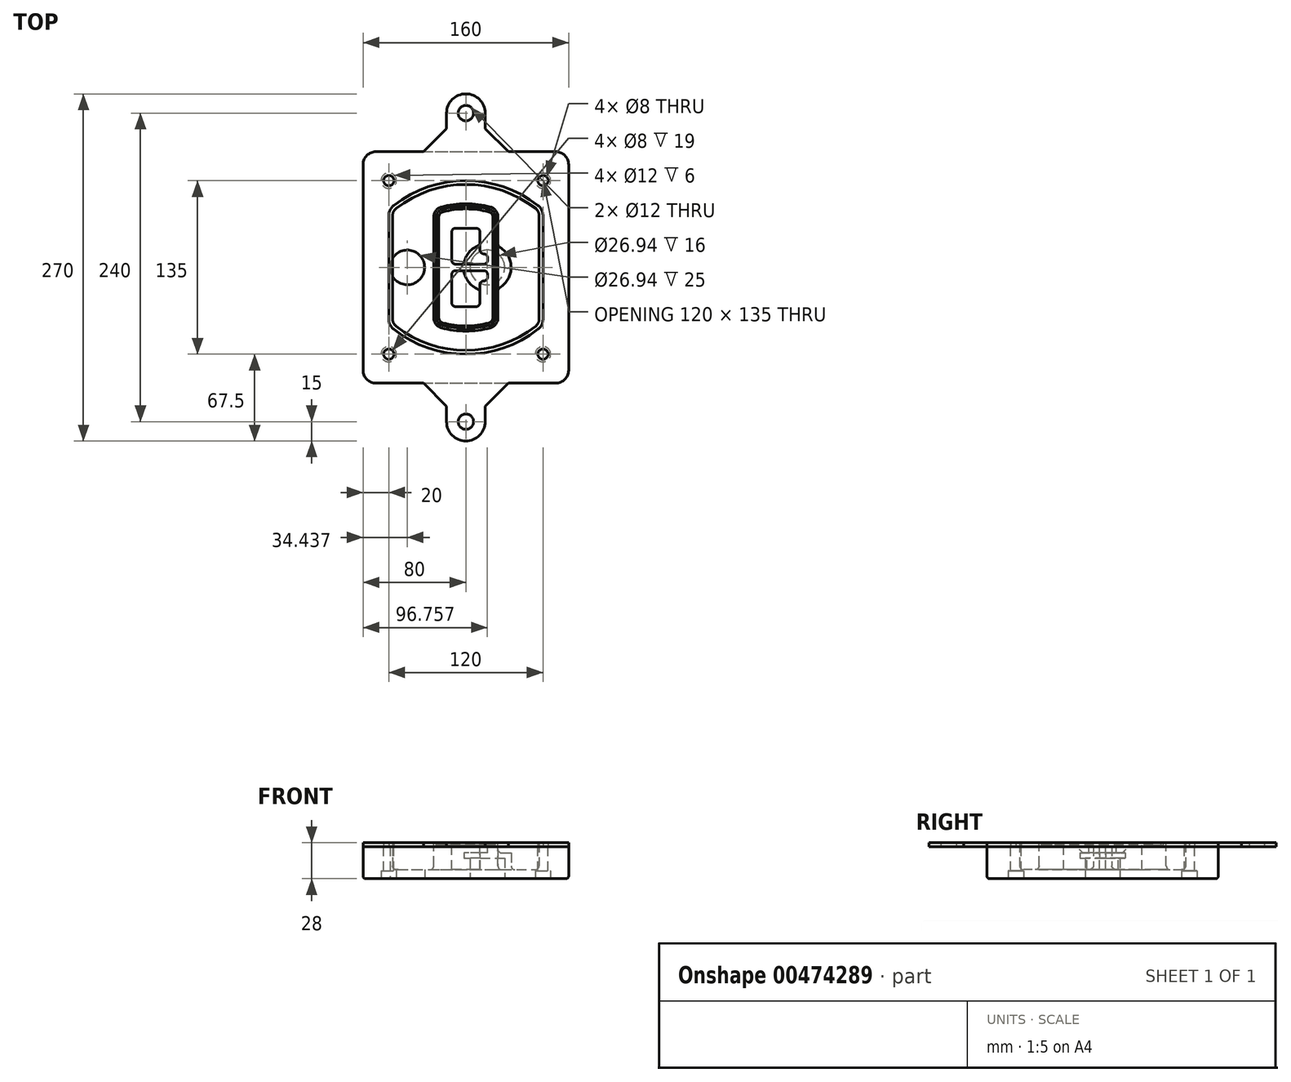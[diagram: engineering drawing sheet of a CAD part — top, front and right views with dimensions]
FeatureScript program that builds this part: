
annotation { "Feature Type Name" : "Feature", "Feature Type Description" : "" }
export const myFeature = defineFeature(function(context is Context, id is Id, definition is map)
    precondition{}
    {
        {
            var Q0;
            Q0=qCreatedBy(makeId("Top.planeOp"),FACE);
            var sketch = newSketch(context, id + "F0", { "sketchPlane" : qUnion([Q0])});
            skPoint(sketch, "E0.rect.middle", {"position": v(0, 0) * mm});
            skLineSegment(sketch, "E1.bottom", {"start": v(-70, -90) * mm, "end": v(70, -90) * mm});
            skLineSegment(sketch, "E1.top", {"start": v(-70, 90) * mm, "end": v(70, 90) * mm});
            skLineSegment(sketch, "E1.left", {"start": v(-80, -80) * mm, "end": v(-80, 80) * mm});
            skLineSegment(sketch, "E1.right", {"start": v(80, -80) * mm, "end": v(80, 80) * mm});
            skLineSegment(sketch, "E2", {"start": v(-80, 90) * mm, "end": v(80, -90) * mm, "construction": true});
            skLineSegment(sketch, "E3", {"start": v(80, 90) * mm, "end": v(-80, -90) * mm, "construction": true});
            skCircle(sketch, "E4", {"center": v(-60, 67.5) * mm, "radius": 4 * mm});
            skCircle(sketch, "E5", {"center": v(60, 67.5) * mm, "radius": 4 * mm});
            skCircle(sketch, "E6", {"center": v(60, -67.5) * mm, "radius": 4 * mm});
            skCircle(sketch, "E7", {"center": v(-60, -67.5) * mm, "radius": 4 * mm});
            skLineSegment(sketch, "E8", {"start": v(-60, 67.5) * mm, "end": v(60, 67.5) * mm, "construction": true});
            skLineSegment(sketch, "E9", {"start": v(60, 67.5) * mm, "end": v(60, -67.5) * mm, "construction": true});
            skLineSegment(sketch, "E10", {"start": v(60, -67.5) * mm, "end": v(-60, -67.5) * mm, "construction": true});
            skLineSegment(sketch, "E11", {"start": v(-60, -67.5) * mm, "end": v(-60, 67.5) * mm, "construction": true});
            skLineSegment(sketch, "E12", {"start": v(-60, 40.3) * mm, "end": v(-60, -40.3) * mm});
            skLineSegment(sketch, "E13", {"start": v(60, 40.3) * mm, "end": v(60, -40.3) * mm});
            skArc(sketch, "E14", {"start": v(56.15, 48.18) * mm, "mid": v(0, 67.5) * mm, "end": v(-56.15, 48.18) * mm});
            skArc(sketch, "E15", {"start": v(-56.15, -48.18) * mm, "mid": v(0, -67.5) * mm, "end": v(56.15, -48.18) * mm});
            skLineSegment(sketch, "E16", {"start": v(-60, 0) * mm, "end": v(60, 0) * mm, "construction": true});
            skPoint(sketch, "E17.visualSharp", {"position": v(-60, -45) * mm});
            skArc(sketch, "E17.filletArc", {"start": v(-60, -40.3) * mm, "mid": v(-58.99, -44.68) * mm, "end": v(-56.15, -48.18) * mm});
            skPoint(sketch, "E18.visualSharp", {"position": v(-60, 45) * mm});
            skArc(sketch, "E18.filletArc", {"start": v(-56.15, 48.18) * mm, "mid": v(-58.99, 44.68) * mm, "end": v(-60, 40.3) * mm});
            skPoint(sketch, "E19.visualSharp", {"position": v(60, 45) * mm});
            skArc(sketch, "E19.filletArc", {"start": v(60, 40.3) * mm, "mid": v(58.99, 44.68) * mm, "end": v(56.15, 48.18) * mm});
            skPoint(sketch, "E20.visualSharp", {"position": v(60, -45) * mm});
            skArc(sketch, "E20.filletArc", {"start": v(56.15, -48.18) * mm, "mid": v(58.99, -44.68) * mm, "end": v(60, -40.3) * mm});
            skPoint(sketch, "E21.visualSharp", {"position": v(-80, 90) * mm});
            skArc(sketch, "E21.filletArc", {"start": v(-70, 90) * mm, "mid": v(-77.07, 87.07) * mm, "end": v(-80, 80) * mm});
            skPoint(sketch, "E22.visualSharp", {"position": v(80, 90) * mm});
            skArc(sketch, "E22.filletArc", {"start": v(80, 80) * mm, "mid": v(77.07, 87.07) * mm, "end": v(70, 90) * mm});
            skPoint(sketch, "E23.visualSharp", {"position": v(80, -90) * mm});
            skArc(sketch, "E23.filletArc", {"start": v(70, -90) * mm, "mid": v(77.07, -87.07) * mm, "end": v(80, -80) * mm});
            skPoint(sketch, "E24.visualSharp", {"position": v(-80, -90) * mm});
            skArc(sketch, "E24.filletArc", {"start": v(-80, -80) * mm, "mid": v(-77.07, -87.07) * mm, "end": v(-70, -90) * mm});
            skArc(sketch, "E25.0", {"start": v(57, 40.3) * mm, "mid": v(56.3, 43.36) * mm, "end": v(54.3, 45.81) * mm});
            skLineSegment(sketch, "E25.1", {"start": v(57, 40.3) * mm, "end": v(57, -40.3) * mm});
            skArc(sketch, "E25.2", {"start": v(54.3, -45.81) * mm, "mid": v(56.3, -43.36) * mm, "end": v(57, -40.3) * mm});
            skArc(sketch, "E25.3", {"start": v(-54.3, -45.81) * mm, "mid": v(0, -64.5) * mm, "end": v(54.3, -45.81) * mm});
            skArc(sketch, "E25.4", {"start": v(-57, -40.3) * mm, "mid": v(-56.3, -43.36) * mm, "end": v(-54.3, -45.81) * mm});
            skArc(sketch, "E25.5", {"start": v(54.3, 45.81) * mm, "mid": v(0, 64.5) * mm, "end": v(-54.3, 45.81) * mm});
            skLineSegment(sketch, "E25.6", {"start": v(-57, 40.3) * mm, "end": v(-57, -40.3) * mm});
            skArc(sketch, "E25.7", {"start": v(-54.3, 45.81) * mm, "mid": v(-56.3, 43.36) * mm, "end": v(-57, 40.3) * mm});
            skArc(sketch, "E26.0", {"start": v(-58.62, 51.33) * mm, "mid": v(-62.58, 46.43) * mm, "end": v(-64, 40.3) * mm});
            skArc(sketch, "E26.1", {"start": v(58.62, 51.33) * mm, "mid": v(0, 71.5) * mm, "end": v(-58.62, 51.33) * mm});
            skArc(sketch, "E26.2", {"start": v(64, 40.3) * mm, "mid": v(62.58, 46.43) * mm, "end": v(58.62, 51.33) * mm});
            skLineSegment(sketch, "E26.3", {"start": v(64, 40.3) * mm, "end": v(64, -40.3) * mm});
            skArc(sketch, "E26.4", {"start": v(58.62, -51.33) * mm, "mid": v(62.58, -46.43) * mm, "end": v(64, -40.3) * mm});
            skLineSegment(sketch, "E26.5", {"start": v(-64, 40.3) * mm, "end": v(-64, -40.3) * mm});
            skArc(sketch, "E26.6", {"start": v(-58.62, -51.33) * mm, "mid": v(0, -71.5) * mm, "end": v(58.62, -51.33) * mm});
            skArc(sketch, "E26.7", {"start": v(-64, -40.3) * mm, "mid": v(-62.58, -46.43) * mm, "end": v(-58.62, -51.33) * mm});
            skSolve(sketch);
        }
        {
            var Q0;
            Q0=makeQuery(id+"F0.imprint","IMPRINT",FACE,{"disambiguationData":[TD([[makeQuery(id+"F0.imprint","IMPRINT",EDGE,{"derivedFrom":sQuery(id+"F0.wireOp",EDGE,"E1.bottom")}),1.0]])]});
            var Q1;
            Q1=makeQuery(id+"F0.imprint","IMPRINT",FACE,{"disambiguationData":[TD([[makeQuery(id+"F0.imprint","IMPRINT",EDGE,{"derivedFrom":sQuery(id+"F0.wireOp",EDGE,"E12")}),1.0]])]});
            var Q2;
            Q2=makeQuery(id+"F0.imprint","IMPRINT",FACE,{"disambiguationData":[TD([[makeQuery(id+"F0.imprint","IMPRINT",EDGE,{"derivedFrom":sQuery(id+"F0.wireOp",EDGE,"E25.0")}),1.0]])]});
            var Q3;
            Q3=makeQuery(id+"F0.imprint","IMPRINT",FACE,{"disambiguationData":[TD([[makeQuery(id+"F0.imprint","IMPRINT",EDGE,{"derivedFrom":sQuery(id+"F0.wireOp",EDGE,"E12")}),-1.0]])]});
            extrude(context, id + "F1", {"entities" : qUnion([Q0, Q1, Q2, Q3]), "oppositeDirection" : true, "depth" : 25 * mm});
        }
        {
            var Q0;
            Q0=makeQuery(id+"F0.imprint","IMPRINT",FACE,{"disambiguationData":[TD([[makeQuery(id+"F0.imprint","IMPRINT",EDGE,{"derivedFrom":sQuery(id+"F0.wireOp",EDGE,"E12")}),1.0]])]});
            extrude(context, id + "F2", {"entities" : qUnion([Q0]), "operationType" : NewBodyOperationType.ADD, "depth" : 3 * mm});
        }
        {
            var Q0;
            Q0=makeQuery(id+"F0.imprint","IMPRINT",FACE,{"disambiguationData":[TD([[makeQuery(id+"F0.imprint","IMPRINT",EDGE,{"derivedFrom":sQuery(id+"F0.wireOp",EDGE,"E25.0")}),1.0]])]});
            extrude(context, id + "F3", {"entities" : qUnion([Q0]), "operationType" : NewBodyOperationType.REMOVE, "oppositeDirection" : true, "depth" : 18 * mm});
        }
        {
            var Q0;
            Q0=makeQuery(id+"F2.opExtrude","CAP_FACE",FACE,{"disambiguationData":[OSD([sQuery(id+"F0.wireOp",EDGE,"E12"),sQuery(id+"F0.wireOp",EDGE,"E13"),sQuery(id+"F0.wireOp",EDGE,"E14"),sQuery(id+"F0.wireOp",EDGE,"E15"),sQuery(id+"F0.wireOp",EDGE,"E17.filletArc"),sQuery(id+"F0.wireOp",EDGE,"E18.filletArc"),sQuery(id+"F0.wireOp",EDGE,"E19.filletArc"),sQuery(id+"F0.wireOp",EDGE,"E20.filletArc"),sQuery(id+"F0.wireOp",EDGE,"E25.0"),sQuery(id+"F0.wireOp",EDGE,"E25.1"),sQuery(id+"F0.wireOp",EDGE,"E25.2"),sQuery(id+"F0.wireOp",EDGE,"E25.3"),sQuery(id+"F0.wireOp",EDGE,"E25.4"),sQuery(id+"F0.wireOp",EDGE,"E25.5"),sQuery(id+"F0.wireOp",EDGE,"E25.6"),sQuery(id+"F0.wireOp",EDGE,"E25.7")])],"isStart":false});
            var sketch = newSketch(context, id + "F4", { "sketchPlane" : qUnion([Q0])});
            skArc(sketch, "E27.0", {"start": v(-19.08, -46.97) * mm, "mid": v(0, -49.5) * mm, "end": v(19.08, -46.97) * mm});
            skArc(sketch, "E28.0", {"start": v(19.08, 46.97) * mm, "mid": v(0, 49.5) * mm, "end": v(-19.08, 46.97) * mm});
            skLineSegment(sketch, "E29", {"start": v(-25, 39.25) * mm, "end": v(-25, -39.25) * mm});
            skLineSegment(sketch, "E30", {"start": v(25, 39.25) * mm, "end": v(25, -39.25) * mm});
            skLineSegment(sketch, "E31", {"start": v(-25, 45.1) * mm, "end": v(25, 45.1) * mm, "construction": true});
            skLineSegment(sketch, "E32", {"start": v(-25, -45.1) * mm, "end": v(25, -45.1) * mm, "construction": true});
            skPoint(sketch, "E33.visualSharp", {"position": v(-25, 45.1) * mm});
            skArc(sketch, "E33.filletArc", {"start": v(-19.08, 46.97) * mm, "mid": v(-23.35, 44.11) * mm, "end": v(-25, 39.25) * mm});
            skPoint(sketch, "E34.visualSharp", {"position": v(25, 45.1) * mm});
            skArc(sketch, "E34.filletArc", {"start": v(25, 39.25) * mm, "mid": v(23.35, 44.11) * mm, "end": v(19.08, 46.97) * mm});
            skPoint(sketch, "E35.visualSharp", {"position": v(25, -45.1) * mm});
            skArc(sketch, "E35.filletArc", {"start": v(19.08, -46.97) * mm, "mid": v(23.35, -44.11) * mm, "end": v(25, -39.25) * mm});
            skPoint(sketch, "E36.visualSharp", {"position": v(-25, -45.1) * mm});
            skArc(sketch, "E36.filletArc", {"start": v(-25, -39.25) * mm, "mid": v(-23.35, -44.11) * mm, "end": v(-19.08, -46.97) * mm});
            skArc(sketch, "E37.0", {"start": v(54.3, 45.81) * mm, "mid": v(0, 64.5) * mm, "end": v(-54.3, 45.81) * mm});
            skArc(sketch, "E37.1", {"start": v(-54.3, 45.81) * mm, "mid": v(-56.3, 43.36) * mm, "end": v(-57, 40.3) * mm});
            skLineSegment(sketch, "E37.2", {"start": v(-57, 40.3) * mm, "end": v(-57, -40.3) * mm});
            skArc(sketch, "E37.3", {"start": v(-57, -40.3) * mm, "mid": v(-56.3, -43.36) * mm, "end": v(-54.3, -45.81) * mm});
            skArc(sketch, "E37.4", {"start": v(-54.3, -45.81) * mm, "mid": v(0, -64.5) * mm, "end": v(54.3, -45.81) * mm});
            skArc(sketch, "E37.5", {"start": v(54.3, -45.81) * mm, "mid": v(56.3, -43.36) * mm, "end": v(57, -40.3) * mm});
            skLineSegment(sketch, "E37.6", {"start": v(57, 40.3) * mm, "end": v(57, -40.3) * mm});
            skArc(sketch, "E37.7", {"start": v(57, 40.3) * mm, "mid": v(56.3, 43.36) * mm, "end": v(54.3, 45.81) * mm});
            skLineSegment(sketch, "E38.0", {"start": v(23, 39.25) * mm, "end": v(23, -39.25) * mm});
            skArc(sketch, "E38.1", {"start": v(18.56, -45.04) * mm, "mid": v(21.76, -42.9) * mm, "end": v(23, -39.25) * mm});
            skArc(sketch, "E38.2", {"start": v(-18.56, -45.04) * mm, "mid": v(0, -47.5) * mm, "end": v(18.56, -45.04) * mm});
            skArc(sketch, "E38.3", {"start": v(-23, -39.25) * mm, "mid": v(-21.76, -42.9) * mm, "end": v(-18.56, -45.04) * mm});
            skLineSegment(sketch, "E38.4", {"start": v(-23, 39.25) * mm, "end": v(-23, -39.25) * mm});
            skArc(sketch, "E38.5", {"start": v(23, 39.25) * mm, "mid": v(21.76, 42.9) * mm, "end": v(18.56, 45.04) * mm});
            skArc(sketch, "E38.6", {"start": v(-18.56, 45.04) * mm, "mid": v(-21.76, 42.9) * mm, "end": v(-23, 39.25) * mm});
            skArc(sketch, "E38.7", {"start": v(18.56, 45.04) * mm, "mid": v(0, 47.5) * mm, "end": v(-18.56, 45.04) * mm});
            skArc(sketch, "E39.0", {"start": v(21, 39.25) * mm, "mid": v(20.18, 41.68) * mm, "end": v(18.04, 43.1) * mm});
            skLineSegment(sketch, "E39.1", {"start": v(21, 39.25) * mm, "end": v(21, -39.25) * mm});
            skArc(sketch, "E39.2", {"start": v(18.04, -43.1) * mm, "mid": v(20.18, -41.68) * mm, "end": v(21, -39.25) * mm});
            skArc(sketch, "E39.3", {"start": v(-18.04, -43.1) * mm, "mid": v(0, -45.5) * mm, "end": v(18.04, -43.1) * mm});
            skArc(sketch, "E39.4", {"start": v(-21, -39.25) * mm, "mid": v(-20.18, -41.68) * mm, "end": v(-18.04, -43.1) * mm});
            skArc(sketch, "E39.5", {"start": v(18.04, 43.1) * mm, "mid": v(0, 45.5) * mm, "end": v(-18.04, 43.1) * mm});
            skLineSegment(sketch, "E39.6", {"start": v(-21, 39.25) * mm, "end": v(-21, -39.25) * mm});
            skArc(sketch, "E39.7", {"start": v(-18.04, 43.1) * mm, "mid": v(-20.18, 41.68) * mm, "end": v(-21, 39.25) * mm});
            skLineSegment(sketch, "E40", {"start": v(-25, 0) * mm, "end": v(25, 0) * mm, "construction": true});
            skLineSegment(sketch, "E41", {"start": v(-11, 5.5) * mm, "end": v(-11, 27.5) * mm});
            skLineSegment(sketch, "E42", {"start": v(-8, 30.5) * mm, "end": v(8, 30.5) * mm});
            skLineSegment(sketch, "E43", {"start": v(11, 27.5) * mm, "end": v(11, 13.5) * mm});
            skLineSegment(sketch, "E44", {"start": v(14, 10.5) * mm, "end": v(14, 10.5) * mm});
            skLineSegment(sketch, "E45", {"start": v(17, 7.5) * mm, "end": v(17, 5.5) * mm});
            skLineSegment(sketch, "E46", {"start": v(14, 2.5) * mm, "end": v(-8, 2.5) * mm});
            skPoint(sketch, "E47.visualSharp", {"position": v(-11, 30.5) * mm});
            skArc(sketch, "E47.filletArc", {"start": v(-8, 30.5) * mm, "mid": v(-10.12, 29.62) * mm, "end": v(-11, 27.5) * mm});
            skPoint(sketch, "E48.visualSharp", {"position": v(11, 30.5) * mm});
            skArc(sketch, "E48.filletArc", {"start": v(11, 27.5) * mm, "mid": v(10.12, 29.62) * mm, "end": v(8, 30.5) * mm});
            skPoint(sketch, "E49.visualSharp", {"position": v(11, 10.5) * mm});
            skArc(sketch, "E49.filletArc", {"start": v(11, 13.5) * mm, "mid": v(11.88, 11.38) * mm, "end": v(14, 10.5) * mm});
            skPoint(sketch, "E50.visualSharp", {"position": v(17, 10.5) * mm});
            skArc(sketch, "E50.filletArc", {"start": v(17, 7.5) * mm, "mid": v(16.12, 9.62) * mm, "end": v(14, 10.5) * mm});
            skPoint(sketch, "E51.visualSharp", {"position": v(17, 2.5) * mm});
            skArc(sketch, "E51.filletArc", {"start": v(14, 2.5) * mm, "mid": v(16.12, 3.38) * mm, "end": v(17, 5.5) * mm});
            skPoint(sketch, "E52.visualSharp", {"position": v(-11, 2.5) * mm});
            skArc(sketch, "E52.filletArc", {"start": v(-11, 5.5) * mm, "mid": v(-10.12, 3.38) * mm, "end": v(-8, 2.5) * mm});
            skLineSegment(sketch, "E53.0.MirrorCS", {"start": v(14, -2.5) * mm, "end": v(-8, -2.5) * mm});
            skArc(sketch, "E54.0.MirrorCS", {"start": v(-11, -5.5) * mm, "mid": v(-10.12, -3.38) * mm, "end": v(-8, -2.5) * mm});
            skLineSegment(sketch, "E55.0.MirrorCS", {"start": v(-11, -5.5) * mm, "end": v(-11, -27.5) * mm});
            skArc(sketch, "E56.0.MirrorCS", {"start": v(-8, -30.5) * mm, "mid": v(-10.12, -29.62) * mm, "end": v(-11, -27.5) * mm});
            skLineSegment(sketch, "E57.0.MirrorCS", {"start": v(-8, -30.5) * mm, "end": v(8, -30.5) * mm});
            skArc(sketch, "E58.0.MirrorCS", {"start": v(11, -27.5) * mm, "mid": v(10.12, -29.62) * mm, "end": v(8, -30.5) * mm});
            skLineSegment(sketch, "E59.0.MirrorCS", {"start": v(11, -27.5) * mm, "end": v(11, -13.5) * mm});
            skArc(sketch, "E60.0.MirrorCS", {"start": v(11, -13.5) * mm, "mid": v(11.88, -11.38) * mm, "end": v(14, -10.5) * mm});
            skArc(sketch, "E61.0.MirrorCS", {"start": v(17, -7.5) * mm, "mid": v(16.12, -9.62) * mm, "end": v(14, -10.5) * mm});
            skLineSegment(sketch, "E62.0.MirrorCS", {"start": v(17, -7.5) * mm, "end": v(17, -5.5) * mm});
            skArc(sketch, "E63.0.MirrorCS", {"start": v(14, -2.5) * mm, "mid": v(16.12, -3.38) * mm, "end": v(17, -5.5) * mm});
            skSolve(sketch);
        }
        {
            var Q0;
            Q0=makeQuery(id+"F4.imprint","IMPRINT",FACE,{"disambiguationData":[TD([[makeQuery(id+"F4.imprint","IMPRINT",EDGE,{"derivedFrom":sQuery(id+"F4.wireOp",EDGE,"E27.0")}),1.0]])]});
            var Q1;
            Q1=makeQuery(id+"F4.imprint","IMPRINT",FACE,{"disambiguationData":[TD([[makeQuery(id+"F4.imprint","IMPRINT",EDGE,{"derivedFrom":sQuery(id+"F4.wireOp",EDGE,"E38.0")}),-1.0]])]});
            var Q2;
            Q2=makeQuery(id+"F4.imprint","IMPRINT",FACE,{"disambiguationData":[TD([[makeQuery(id+"F4.imprint","IMPRINT",EDGE,{"derivedFrom":sQuery(id+"F4.wireOp",EDGE,"E39.0")}),1.0]])]});
            extrude(context, id + "F5", {"entities" : qUnion([Q0, Q1, Q2]), "operationType" : NewBodyOperationType.ADD, "endBound" : BoundingType.UP_TO_NEXT, "oppositeDirection" : true, "depth" : 25 * mm});
        }
        {
            var Q0;
            Q0=makeQuery(id+"F4.imprint","IMPRINT",FACE,{"disambiguationData":[TD([[makeQuery(id+"F4.imprint","IMPRINT",EDGE,{"derivedFrom":sQuery(id+"F4.wireOp",EDGE,"E38.0")}),-1.0]])]});
            extrude(context, id + "F6", {"entities" : qUnion([Q0]), "operationType" : NewBodyOperationType.REMOVE, "oppositeDirection" : true, "depth" : 2 * mm});
        }
        {
            var Q0;
            Q0=makeQuery(id+"F1.opExtrude","CAP_FACE",FACE,{"disambiguationData":[OSD([sQuery(id+"F0.wireOp",EDGE,"E1.bottom"),sQuery(id+"F0.wireOp",EDGE,"E1.top"),sQuery(id+"F0.wireOp",EDGE,"E1.left"),sQuery(id+"F0.wireOp",EDGE,"E1.right"),sQuery(id+"F0.wireOp",EDGE,"E4"),sQuery(id+"F0.wireOp",EDGE,"E5"),sQuery(id+"F0.wireOp",EDGE,"E6"),sQuery(id+"F0.wireOp",EDGE,"E7"),sQuery(id+"F0.wireOp",EDGE,"E21.filletArc"),sQuery(id+"F0.wireOp",EDGE,"E22.filletArc"),sQuery(id+"F0.wireOp",EDGE,"E23.filletArc"),sQuery(id+"F0.wireOp",EDGE,"E24.filletArc")])],"isStart":false});
            var sketch = newSketch(context, id + "F7", { "sketchPlane" : qUnion([Q0])});
            skCircle(sketch, "E64", {"center": v(16.76, 0) * mm, "radius": 13.47 * mm});
            skCircle(sketch, "E65", {"center": v(-45.56, 0) * mm, "radius": 13.47 * mm});
            skLineSegment(sketch, "E66", {"start": v(80, 0) * mm, "end": v(-80, 0) * mm});
            skCircle(sketch, "E67", {"center": v(16.76, 0) * mm, "radius": 18.47 * mm});
            skCircle(sketch, "E68", {"center": v(60, -67.5) * mm, "radius": 6 * mm});
            skCircle(sketch, "E69", {"center": v(-60, -67.5) * mm, "radius": 6 * mm});
            skCircle(sketch, "E70", {"center": v(-60, 67.5) * mm, "radius": 6 * mm});
            skCircle(sketch, "E71", {"center": v(60, 67.5) * mm, "radius": 6 * mm});
            skSolve(sketch);
        }
        {
            var Q0;
            {var subQ1=sQuery(id+"F7.wireOp",EDGE,"E66");var subQ4=sQuery(id+"F7.wireOp",EDGE,"E64");var subQ6=makeQuery(id+"F7.imprint","INTERSECT",VERTEX,{"disambiguationData":[OD(0.0)],"derivedFrom":[subQ4,subQ1]});Q0=makeQuery(id+"F7.imprint","IMPRINT",FACE,{"disambiguationData":[TD([[makeQuery(id+"F7.imprint","IMPRINT",EDGE,{"disambiguationData":[TD([[subQ6,-1.0]])],"derivedFrom":subQ4}),-1.0]])]});}
            var Q1;
            {var subQ0=sQuery(id+"F7.wireOp",EDGE,"E66");var subQ1=sQuery(id+"F7.wireOp",EDGE,"E64");var subQ3=makeQuery(id+"F7.imprint","INTERSECT",VERTEX,{"disambiguationData":[OD(0.0)],"derivedFrom":[subQ1,subQ0]});Q1=makeQuery(id+"F7.imprint","IMPRINT",FACE,{"disambiguationData":[TD([[makeQuery(id+"F7.imprint","IMPRINT",EDGE,{"disambiguationData":[TD([[subQ3,-1.0]])],"derivedFrom":subQ1}),1.0]])]});}
            var Q2;
            {var subQ0=sQuery(id+"F7.wireOp",EDGE,"E66");var subQ1=sQuery(id+"F7.wireOp",EDGE,"E64");var subQ3=makeQuery(id+"F7.imprint","INTERSECT",VERTEX,{"disambiguationData":[OD(0.0)],"derivedFrom":[subQ1,subQ0]});Q2=makeQuery(id+"F7.imprint","IMPRINT",FACE,{"disambiguationData":[TD([[makeQuery(id+"F7.imprint","IMPRINT",EDGE,{"disambiguationData":[TD([[subQ3,1.0]])],"derivedFrom":subQ1}),1.0]])]});}
            var Q3;
            {var subQ1=sQuery(id+"F7.wireOp",EDGE,"E66");var subQ4=sQuery(id+"F7.wireOp",EDGE,"E64");var subQ6=makeQuery(id+"F7.imprint","INTERSECT",VERTEX,{"disambiguationData":[OD(0.0)],"derivedFrom":[subQ4,subQ1]});Q3=makeQuery(id+"F7.imprint","IMPRINT",FACE,{"disambiguationData":[TD([[makeQuery(id+"F7.imprint","IMPRINT",EDGE,{"disambiguationData":[TD([[subQ6,1.0]])],"derivedFrom":subQ4}),-1.0]])]});}
            extrude(context, id + "F8", {"entities" : qUnion([Q0, Q1, Q2, Q3]), "operationType" : NewBodyOperationType.ADD, "oppositeDirection" : true, "depth" : 20 * mm});
        }
        {
            var Q0;
            {var subQ0=sQuery(id+"F7.wireOp",EDGE,"E66");var subQ1=sQuery(id+"F7.wireOp",EDGE,"E64");var subQ3=makeQuery(id+"F7.imprint","INTERSECT",VERTEX,{"disambiguationData":[OD(0.0)],"derivedFrom":[subQ1,subQ0]});Q0=makeQuery(id+"F7.imprint","IMPRINT",FACE,{"disambiguationData":[TD([[makeQuery(id+"F7.imprint","IMPRINT",EDGE,{"disambiguationData":[TD([[subQ3,-1.0]])],"derivedFrom":subQ1}),1.0]])]});}
            var Q1;
            {var subQ0=sQuery(id+"F7.wireOp",EDGE,"E66");var subQ1=sQuery(id+"F7.wireOp",EDGE,"E64");var subQ3=makeQuery(id+"F7.imprint","INTERSECT",VERTEX,{"disambiguationData":[OD(0.0)],"derivedFrom":[subQ1,subQ0]});Q1=makeQuery(id+"F7.imprint","IMPRINT",FACE,{"disambiguationData":[TD([[makeQuery(id+"F7.imprint","IMPRINT",EDGE,{"disambiguationData":[TD([[subQ3,1.0]])],"derivedFrom":subQ1}),1.0]])]});}
            extrude(context, id + "F9", {"entities" : qUnion([Q0, Q1]), "operationType" : NewBodyOperationType.REMOVE, "oppositeDirection" : true, "depth" : 16 * mm});
        }
        {
            var Q0;
            {var subQ0=sQuery(id+"F7.wireOp",EDGE,"E66");var subQ1=sQuery(id+"F7.wireOp",EDGE,"E65");var subQ3=makeQuery(id+"F7.imprint","INTERSECT",VERTEX,{"disambiguationData":[OD(0.0)],"derivedFrom":[subQ1,subQ0]});Q0=makeQuery(id+"F7.imprint","IMPRINT",FACE,{"disambiguationData":[TD([[makeQuery(id+"F7.imprint","IMPRINT",EDGE,{"disambiguationData":[TD([[subQ3,-1.0]])],"derivedFrom":subQ1}),1.0]])]});}
            var Q1;
            {var subQ0=sQuery(id+"F7.wireOp",EDGE,"E66");var subQ1=sQuery(id+"F7.wireOp",EDGE,"E65");var subQ3=makeQuery(id+"F7.imprint","INTERSECT",VERTEX,{"disambiguationData":[OD(0.0)],"derivedFrom":[subQ1,subQ0]});Q1=makeQuery(id+"F7.imprint","IMPRINT",FACE,{"disambiguationData":[TD([[makeQuery(id+"F7.imprint","IMPRINT",EDGE,{"disambiguationData":[TD([[subQ3,1.0]])],"derivedFrom":subQ1}),1.0]])]});}
            extrude(context, id + "F10", {"entities" : qUnion([Q0, Q1]), "operationType" : NewBodyOperationType.REMOVE, "oppositeDirection" : true, "depth" : 25 * mm});
        }
        {
            var Q0;
            Q0=makeQuery(id+"F7.imprint","IMPRINT",FACE,{"disambiguationData":[TD([[makeQuery(id+"F7.imprint","IMPRINT",EDGE,{"derivedFrom":sQuery(id+"F7.wireOp",EDGE,"E68")}),1.0]])]});
            var Q1;
            Q1=makeQuery(id+"F7.imprint","IMPRINT",FACE,{"disambiguationData":[TD([[makeQuery(id+"F7.imprint","IMPRINT",EDGE,{"derivedFrom":makeQuery(id+"F1.opExtrude","CAP_EDGE",EDGE,{"disambiguationData":[OSD([sQuery(id+"F0.wireOp",EDGE,"E5")])],"isStart":false})}),-1.0]])]});
            var Q2;
            Q2=makeQuery(id+"F7.imprint","IMPRINT",FACE,{"disambiguationData":[TD([[makeQuery(id+"F7.imprint","IMPRINT",EDGE,{"derivedFrom":sQuery(id+"F7.wireOp",EDGE,"E69")}),1.0]])]});
            var Q3;
            Q3=makeQuery(id+"F7.imprint","IMPRINT",FACE,{"disambiguationData":[TD([[makeQuery(id+"F7.imprint","IMPRINT",EDGE,{"derivedFrom":makeQuery(id+"F1.opExtrude","CAP_EDGE",EDGE,{"disambiguationData":[OSD([sQuery(id+"F0.wireOp",EDGE,"E4")])],"isStart":false})}),-1.0]])]});
            var Q4;
            Q4=makeQuery(id+"F7.imprint","IMPRINT",FACE,{"disambiguationData":[TD([[makeQuery(id+"F7.imprint","IMPRINT",EDGE,{"derivedFrom":sQuery(id+"F7.wireOp",EDGE,"E70")}),1.0]])]});
            var Q5;
            Q5=makeQuery(id+"F7.imprint","IMPRINT",FACE,{"disambiguationData":[TD([[makeQuery(id+"F7.imprint","IMPRINT",EDGE,{"derivedFrom":makeQuery(id+"F1.opExtrude","CAP_EDGE",EDGE,{"disambiguationData":[OSD([sQuery(id+"F0.wireOp",EDGE,"E7")])],"isStart":false})}),-1.0]])]});
            var Q6;
            Q6=makeQuery(id+"F7.imprint","IMPRINT",FACE,{"disambiguationData":[TD([[makeQuery(id+"F7.imprint","IMPRINT",EDGE,{"derivedFrom":sQuery(id+"F7.wireOp",EDGE,"E71")}),1.0]])]});
            var Q7;
            Q7=makeQuery(id+"F7.imprint","IMPRINT",FACE,{"disambiguationData":[TD([[makeQuery(id+"F7.imprint","IMPRINT",EDGE,{"derivedFrom":makeQuery(id+"F1.opExtrude","CAP_EDGE",EDGE,{"disambiguationData":[OSD([sQuery(id+"F0.wireOp",EDGE,"E6")])],"isStart":false})}),-1.0]])]});
            extrude(context, id + "F11", {"entities" : qUnion([Q0, Q1, Q2, Q3, Q4, Q5, Q6, Q7]), "operationType" : NewBodyOperationType.REMOVE, "oppositeDirection" : true, "depth" : 6 * mm});
        }
        {
            var Q0;
            Q0=makeQuery(id+"F9.boolean.opBoolean","COPY",FACE,{"derivedFrom":makeQuery(id+"F9.opExtrude","CAP_FACE",FACE,{"disambiguationData":[OSD([sQuery(id+"F7.wireOp",EDGE,"E64")])],"isStart":false})});
            var sketch = newSketch(context, id + "F12", { "sketchPlane" : qUnion([Q0])});
            skArc(sketch, "E72.0", {"start": v(11, 17.55) * mm, "mid": v(2.57, 11.82) * mm, "end": v(-1.54, 2.5) * mm});
            skArc(sketch, "E72.1", {"start": v(-1.54, -2.5) * mm, "mid": v(2.57, -11.82) * mm, "end": v(11, -17.55) * mm});
            skLineSegment(sketch, "E73", {"start": v(-1.54, -2.5) * mm, "end": v(14, -2.5) * mm});
            skLineSegment(sketch, "E74.0", {"start": v(14, 2.5) * mm, "end": v(-1.54, 2.5) * mm});
            skArc(sketch, "E74.1", {"start": v(14, 2.5) * mm, "mid": v(16.12, 3.38) * mm, "end": v(17, 5.5) * mm});
            skLineSegment(sketch, "E74.2", {"start": v(17, 7.5) * mm, "end": v(17, 5.5) * mm});
            skArc(sketch, "E74.3", {"start": v(17, 7.5) * mm, "mid": v(16.12, 9.62) * mm, "end": v(14, 10.5) * mm});
            skArc(sketch, "E74.4", {"start": v(11, 13.5) * mm, "mid": v(11.88, 11.38) * mm, "end": v(14, 10.5) * mm});
            skLineSegment(sketch, "E74.5", {"start": v(11, 17.55) * mm, "end": v(11, 13.5) * mm});
            skLineSegment(sketch, "E74.7", {"start": v(14, -2.5) * mm, "end": v(-1.54, -2.5) * mm});
            skArc(sketch, "E74.8", {"start": v(14, -2.5) * mm, "mid": v(16.12, -3.38) * mm, "end": v(17, -5.5) * mm});
            skLineSegment(sketch, "E74.9", {"start": v(17, -7.5) * mm, "end": v(17, -5.5) * mm});
            skArc(sketch, "E74.10", {"start": v(17, -7.5) * mm, "mid": v(16.12, -9.62) * mm, "end": v(14, -10.5) * mm});
            skArc(sketch, "E74.11", {"start": v(11, -13.5) * mm, "mid": v(11.88, -11.38) * mm, "end": v(14, -10.5) * mm});
            skLineSegment(sketch, "E74.12", {"start": v(11, -17.55) * mm, "end": v(11, -13.5) * mm});
            skPoint(sketch, "E75.orphan", {"position": v(11, -27.5) * mm});
            skPoint(sketch, "E76.orphan", {"position": v(-8, -2.5) * mm});
            skPoint(sketch, "E77.orphan", {"position": v(-8, 2.5) * mm});
            skPoint(sketch, "E78.orphan", {"position": v(11, 27.5) * mm});
            skSolve(sketch);
        }
        {
            var Q0;
            {var subQ7=sQuery(id+"F12.wireOp",EDGE,"E72.0");var subQ14=sQuery(id+"F12.wireOp",EDGE,"E72.1");var subQ16=sQuery(id+"F12.wireOp",EDGE,"E74.1");var subQ18=sQuery(id+"F12.wireOp",EDGE,"E74.8");Q0=qUnion([makeQuery(id+"F12.imprint","IMPRINT",FACE,{"disambiguationData":[TD([[makeQuery(id+"F12.imprint","IMPRINT",EDGE,{"derivedFrom":subQ7}),1.0]])]}),makeQuery(id+"F12.imprint","IMPRINT",FACE,{"disambiguationData":[TD([[makeQuery(id+"F12.imprint","IMPRINT",EDGE,{"derivedFrom":subQ14}),1.0]])]}),makeQuery(id+"F12.imprint","IMPRINT",FACE,{"disambiguationData":[TD([[makeQuery(id+"F12.imprint","IMPRINT",EDGE,{"derivedFrom":subQ16}),1.0]])]}),makeQuery(id+"F12.imprint","IMPRINT",FACE,{"disambiguationData":[TD([[makeQuery(id+"F12.imprint","IMPRINT",EDGE,{"derivedFrom":subQ18}),-1.0]])]})]);}
            var Q1;
            Q1=makeQuery(id+"F5.boolean.opBoolean","SPLIT",FACE,{"disambiguationData":[TD([makeQuery(id+"F5.opExtrude","SWEPT_FACE",FACE,{"disambiguationData":[OSD([sQuery(id+"F4.wireOp",EDGE,"E41")])]})])],"derivedFrom":makeQuery(id+"F3.boolean.opBoolean","COPY",FACE,{"derivedFrom":makeQuery(id+"F3.opExtrude","CAP_FACE",FACE,{"disambiguationData":[OSD([sQuery(id+"F0.wireOp",EDGE,"E25.0"),sQuery(id+"F0.wireOp",EDGE,"E25.1"),sQuery(id+"F0.wireOp",EDGE,"E25.2"),sQuery(id+"F0.wireOp",EDGE,"E25.3"),sQuery(id+"F0.wireOp",EDGE,"E25.4"),sQuery(id+"F0.wireOp",EDGE,"E25.5"),sQuery(id+"F0.wireOp",EDGE,"E25.6"),sQuery(id+"F0.wireOp",EDGE,"E25.7")])],"isStart":false})})});
            extrude(context, id + "F13", {"entities" : qUnion([Q0]), "operationType" : NewBodyOperationType.REMOVE, "endBound" : BoundingType.UP_TO_SURFACE, "endBoundEntityFace" : qUnion([Q1]), "depth" : 25 * mm});
        }
        {
            var Q0;
            Q0=makeQuery(id+"F3.boolean.opBoolean","COPY",EDGE,{"derivedFrom":makeQuery(id+"F3.opExtrude","CAP_EDGE",EDGE,{"disambiguationData":[OSD([sQuery(id+"F0.wireOp",EDGE,"E25.6")])],"isStart":false})});
            var Q1;
            Q1=makeQuery(id+"F8.boolean.opBoolean","INTERSECT",EDGE,{"derivedFrom":[makeQuery(id+"F5.opExtrude","SWEPT_FACE",FACE,{"disambiguationData":[OSD([sQuery(id+"F4.wireOp",EDGE,"E30")])]}),makeQuery(id+"F8.opExtrude","CAP_FACE",FACE,{"disambiguationData":[OSD([sQuery(id+"F7.wireOp",EDGE,"E67")])],"isStart":false})]});
            var Q2;
            Q2=makeQuery(id+"F8.boolean.opBoolean","INTERSECT",EDGE,{"disambiguationData":[OD(1.0)],"derivedFrom":[makeQuery(id+"F5.opExtrude","SWEPT_FACE",FACE,{"disambiguationData":[OSD([sQuery(id+"F4.wireOp",EDGE,"E30")])]}),makeQuery(id+"F8.opExtrude","SWEPT_FACE",FACE,{"disambiguationData":[OSD([sQuery(id+"F7.wireOp",EDGE,"E67")])]})]});
            var Q3;
            {var subQ0=sQuery(id+"F4.wireOp",EDGE,"E30");Q3=makeQuery(id+"F8.boolean.opBoolean","SPLIT",EDGE,{"disambiguationData":[TD([makeQuery(id+"F5.opExtrude","SWEPT_FACE",FACE,{"disambiguationData":[OSD([sQuery(id+"F4.wireOp",EDGE,"E35.filletArc")])]})])],"derivedFrom":makeQuery(id+"F5.opExtrude","CAP_EDGE",EDGE,{"disambiguationData":[OSD([subQ0])],"isStart":false})});}
            var Q4;
            {var subQ0=sQuery(id+"F0.wireOp",EDGE,"E25.7");var subQ1=sQuery(id+"F0.wireOp",EDGE,"E25.1");var subQ2=sQuery(id+"F0.wireOp",EDGE,"E25.6");var subQ3=sQuery(id+"F0.wireOp",EDGE,"E25.5");var subQ4=sQuery(id+"F0.wireOp",EDGE,"E25.4");var subQ5=sQuery(id+"F0.wireOp",EDGE,"E25.0");var subQ6=sQuery(id+"F0.wireOp",EDGE,"E25.2");var subQ7=sQuery(id+"F0.wireOp",EDGE,"E25.3");Q4=makeQuery(id+"F8.boolean.opBoolean","INTERSECT",EDGE,{"derivedFrom":[makeQuery(id+"F5.boolean.opBoolean","SPLIT",FACE,{"disambiguationData":[TD([makeQuery(id+"F2.opExtrude","SWEPT_FACE",FACE,{"disambiguationData":[OSD([subQ5])]})])],"derivedFrom":makeQuery(id+"F3.boolean.opBoolean","COPY",FACE,{"derivedFrom":makeQuery(id+"F3.opExtrude","CAP_FACE",FACE,{"disambiguationData":[OSD([subQ5,subQ1,subQ6,subQ7,subQ4,subQ3,subQ2,subQ0])],"isStart":false})})}),makeQuery(id+"F8.opExtrude","SWEPT_FACE",FACE,{"disambiguationData":[OSD([sQuery(id+"F7.wireOp",EDGE,"E67")])]})]});}
            var Q5;
            Q5=makeQuery(id+"F8.boolean.opBoolean","INTERSECT",EDGE,{"disambiguationData":[OD(0.0)],"derivedFrom":[makeQuery(id+"F5.opExtrude","SWEPT_FACE",FACE,{"disambiguationData":[OSD([sQuery(id+"F4.wireOp",EDGE,"E30")])]}),makeQuery(id+"F8.opExtrude","SWEPT_FACE",FACE,{"disambiguationData":[OSD([sQuery(id+"F7.wireOp",EDGE,"E67")])]})]});
            fillet(context, id + "F14", {"entities" : qUnion([Q0, Q1, Q2, Q3, Q4, Q5]), "radius" : 3 * mm, "tangentPropagation" : true, "allowEdgeOverflow" : false});
        }
        {
            var Q0;
            Q0=makeQuery(id+"F1.opExtrude","CAP_EDGE",EDGE,{"disambiguationData":[OSD([sQuery(id+"F0.wireOp",EDGE,"E1.bottom")])],"isStart":false});
            fillet(context, id + "F15", {"entities" : qUnion([Q0]), "radius" : 2 * mm, "tangentPropagation" : true, "allowEdgeOverflow" : false});
        }
        {
            var Q0;
            {var subQ0=sQuery(id+"F0.wireOp",EDGE,"E21.filletArc");var subQ1=sQuery(id+"F0.wireOp",EDGE,"E7");var subQ2=sQuery(id+"F0.wireOp",EDGE,"E6");var subQ3=sQuery(id+"F0.wireOp",EDGE,"E5");var subQ4=sQuery(id+"F0.wireOp",EDGE,"E4");var subQ5=sQuery(id+"F0.wireOp",EDGE,"E22.filletArc");var subQ6=sQuery(id+"F0.wireOp",EDGE,"E1.bottom");var subQ7=sQuery(id+"F0.wireOp",EDGE,"E1.right");var subQ8=sQuery(id+"F0.wireOp",EDGE,"E1.top");var subQ9=sQuery(id+"F0.wireOp",EDGE,"E1.left");var subQ10=sQuery(id+"F0.wireOp",EDGE,"E23.filletArc");var subQ11=sQuery(id+"F0.wireOp",EDGE,"E24.filletArc");Q0=makeQuery(id+"F2.boolean.opBoolean","SPLIT",FACE,{"disambiguationData":[TD([makeQuery(id+"F1.opExtrude","SWEPT_FACE",FACE,{"disambiguationData":[OSD([subQ6])]})])],"derivedFrom":makeQuery(id+"F1.opExtrude","CAP_FACE",FACE,{"disambiguationData":[OSD([subQ6,subQ8,subQ9,subQ7,subQ4,subQ3,subQ2,subQ1,subQ0,subQ5,subQ10,subQ11])],"isStart":true})});}
            var sketch = newSketch(context, id + "F16", { "sketchPlane" : qUnion([Q0])});
            skLineSegment(sketch, "E79.0", {"start": v(-70, 90) * mm, "end": v(70, 90) * mm});
            skArc(sketch, "E80.0", {"start": v(-70, 90) * mm, "mid": v(-77.07, 87.07) * mm, "end": v(-80, 80) * mm});
            skLineSegment(sketch, "E81.0", {"start": v(-80, -80) * mm, "end": v(-80, 80) * mm});
            skArc(sketch, "E82.0", {"start": v(80, 80) * mm, "mid": v(77.07, 87.07) * mm, "end": v(70, 90) * mm});
            skLineSegment(sketch, "E83.0", {"start": v(80, -80) * mm, "end": v(80, 80) * mm});
            skArc(sketch, "E84.0", {"start": v(70, -90) * mm, "mid": v(77.07, -87.07) * mm, "end": v(80, -80) * mm});
            skLineSegment(sketch, "E85.0", {"start": v(-70, -90) * mm, "end": v(70, -90) * mm});
            skCircle(sketch, "E86.0", {"center": v(-60, 67.5) * mm, "radius": 4 * mm});
            skCircle(sketch, "E87.0", {"center": v(-60, -67.5) * mm, "radius": 4 * mm});
            skCircle(sketch, "E88.0", {"center": v(60, -67.5) * mm, "radius": 4 * mm});
            skArc(sketch, "E89.0", {"start": v(-80, -80) * mm, "mid": v(-77.07, -87.07) * mm, "end": v(-70, -90) * mm});
            skArc(sketch, "E90.0", {"start": v(56.15, 48.18) * mm, "mid": v(0, 67.5) * mm, "end": v(-56.15, 48.18) * mm});
            skArc(sketch, "E91.0", {"start": v(-56.15, 48.18) * mm, "mid": v(-58.99, 44.68) * mm, "end": v(-60, 40.3) * mm});
            skLineSegment(sketch, "E92.0", {"start": v(-60, 40.3) * mm, "end": v(-60, -40.3) * mm});
            skArc(sketch, "E93.0", {"start": v(-60, -40.3) * mm, "mid": v(-58.99, -44.68) * mm, "end": v(-56.15, -48.18) * mm});
            skArc(sketch, "E94.0", {"start": v(-56.15, -48.18) * mm, "mid": v(0, -67.5) * mm, "end": v(56.15, -48.18) * mm});
            skArc(sketch, "E95.0", {"start": v(56.15, -48.18) * mm, "mid": v(58.99, -44.68) * mm, "end": v(60, -40.3) * mm});
            skLineSegment(sketch, "E96.0", {"start": v(60, 40.3) * mm, "end": v(60, -40.3) * mm});
            skCircle(sketch, "E97.0", {"center": v(60, 67.5) * mm, "radius": 4 * mm});
            skArc(sketch, "E98.0", {"start": v(60, 40.3) * mm, "mid": v(58.99, 44.68) * mm, "end": v(56.15, 48.18) * mm});
            skLineSegment(sketch, "E99", {"start": v(0, 90) * mm, "end": v(0, 120) * mm, "construction": true});
            skPoint(sketch, "E99.endSnap0", {"position": v(0, 90) * mm});
            skCircle(sketch, "E100", {"center": v(0, 120) * mm, "radius": 6 * mm});
            skArc(sketch, "E101", {"start": v(-15, 120) * mm, "mid": v(0, 135) * mm, "end": v(15, 120) * mm});
            skLineSegment(sketch, "E102", {"start": v(-15, 120) * mm, "end": v(-15, 108) * mm});
            skLineSegment(sketch, "E103", {"start": v(-15, 108) * mm, "end": v(-33, 90) * mm});
            skLineSegment(sketch, "E104.MirrorCS", {"start": v(15, 120) * mm, "end": v(15, 108) * mm});
            skLineSegment(sketch, "E105.MirrorCS", {"start": v(15, 108) * mm, "end": v(33, 90) * mm});
            skLineSegment(sketch, "E106", {"start": v(-80, 0) * mm, "end": v(80, 0) * mm, "construction": true});
            skLineSegment(sketch, "E107.MirrorCS", {"start": v(-15, -108) * mm, "end": v(-33, -90) * mm});
            skLineSegment(sketch, "E108.MirrorCS", {"start": v(-15, -120) * mm, "end": v(-15, -108) * mm});
            skArc(sketch, "E109.MirrorCS", {"start": v(-15, -120) * mm, "mid": v(0, -135) * mm, "end": v(15, -120) * mm});
            skLineSegment(sketch, "E110.MirrorCS", {"start": v(15, -120) * mm, "end": v(15, -108) * mm});
            skLineSegment(sketch, "E111.MirrorCS", {"start": v(15, -108) * mm, "end": v(33, -90) * mm});
            skCircle(sketch, "E112.MirrorC", {"center": v(0, -120) * mm, "radius": 6 * mm});
            skSolve(sketch);
        }
        {
            var Q0;
            Q0 = qSketchRegion(id + "F16", true);
            var Q1;
            Q1=makeQuery(id+"F2.opExtrude","CAP_FACE",FACE,{"disambiguationData":[OSD([sQuery(id+"F0.wireOp",EDGE,"E12"),sQuery(id+"F0.wireOp",EDGE,"E13"),sQuery(id+"F0.wireOp",EDGE,"E14"),sQuery(id+"F0.wireOp",EDGE,"E15"),sQuery(id+"F0.wireOp",EDGE,"E17.filletArc"),sQuery(id+"F0.wireOp",EDGE,"E18.filletArc"),sQuery(id+"F0.wireOp",EDGE,"E19.filletArc"),sQuery(id+"F0.wireOp",EDGE,"E20.filletArc"),sQuery(id+"F0.wireOp",EDGE,"E25.0"),sQuery(id+"F0.wireOp",EDGE,"E25.1"),sQuery(id+"F0.wireOp",EDGE,"E25.2"),sQuery(id+"F0.wireOp",EDGE,"E25.3"),sQuery(id+"F0.wireOp",EDGE,"E25.4"),sQuery(id+"F0.wireOp",EDGE,"E25.5"),sQuery(id+"F0.wireOp",EDGE,"E25.6"),sQuery(id+"F0.wireOp",EDGE,"E25.7")])],"isStart":false});
            extrude(context, id + "F17", {"entities" : qUnion([Q0]), "endBound" : BoundingType.UP_TO_SURFACE, "endBoundEntityFace" : qUnion([Q1]), "depth" : 25 * mm});
        }
    });
